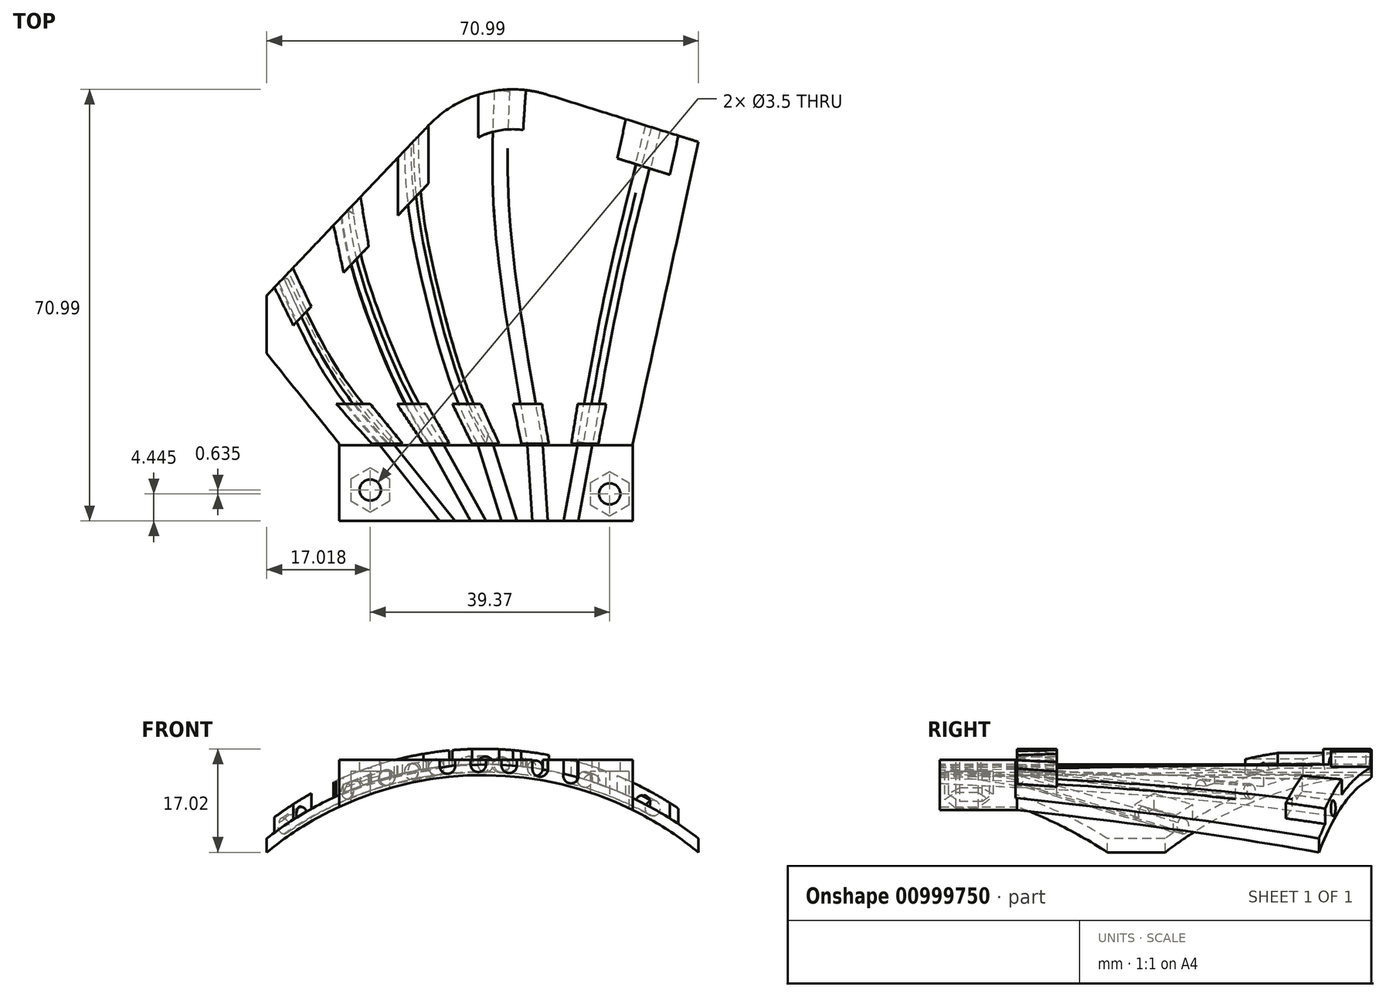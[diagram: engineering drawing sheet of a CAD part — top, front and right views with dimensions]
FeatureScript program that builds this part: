
annotation { "Feature Type Name" : "Feature", "Feature Type Description" : "" }
export const myFeature = defineFeature(function(context is Context, id is Id, definition is map)
    precondition{}
    {
        {
            var Q0;
            Q0=qCreatedBy(makeId("Front.planeOp"),FACE);
            var sketch = newSketch(context, id + "F0", { "sketchPlane" : qUnion([Q0])});
            skLineSegment(sketch, "E0", {"start": v(0, 0) * mm, "end": v(71, 0) * mm});
            skLineSegment(sketch, "E1", {"start": v(35.5, 0) * mm, "end": v(35.5, 12.7) * mm});
            skArc(sketch, "E2", {"start": v(71, 0) * mm, "mid": v(35.5, 12.7) * mm, "end": v(0, 0) * mm});
            skArc(sketch, "E3.0", {"start": v(71, 2.28) * mm, "mid": v(35.5, 14.48) * mm, "end": v(0, 2.28) * mm});
            skLineSegment(sketch, "E4", {"start": v(0, 0) * mm, "end": v(0, 2.28) * mm});
            skLineSegment(sketch, "E5", {"start": v(71, 0) * mm, "end": v(71, 2.28) * mm});
            skSolve(sketch);
        }
        {
            var Q0;
            Q0=makeQuery(id+"F0.imprint","IMPRINT",FACE,{"disambiguationData":[TD([[makeQuery(id+"F0.imprint","IMPRINT",EDGE,{"derivedFrom":sQuery(id+"F0.wireOp",EDGE,"E3.0")}),1.0]])]});
            extrude(context, id + "F1", {"entities" : qUnion([Q0]), "oppositeDirection" : true, "depth" : 63.5 * mm, "offsetDistance" : 25.4 * mm});
        }
        {
            var Q0;
            Q0=qCreatedBy(makeId("Top.planeOp"),FACE);
            cPlane(context, id + "F2", {"entities" : qUnion([Q0]), "cplaneType" : CPlaneType.OFFSET, "offset" : 25.4 * mm, "width" : 152.4 * mm, "height" : 152.4 * mm});
        }
        {
            var Q0;
            Q0=qCreatedBy(id+"F2.planeOp",FACE);
            var sketch = newSketch(context, id + "F3", { "sketchPlane" : qUnion([Q0])});
            skLineSegment(sketch, "E6", {"start": v(11.94, 0) * mm, "end": v(60.2, 0) * mm});
            skLineSegment(sketch, "E7", {"start": v(60.2, 0) * mm, "end": v(71, 49.64) * mm});
            skLineSegment(sketch, "E8", {"start": v(11.94, 0) * mm, "end": v(0, 14.85) * mm});
            skLineSegment(sketch, "E9", {"start": v(0, 14.85) * mm, "end": v(0, 24.37) * mm});
            skLineSegment(sketch, "E10", {"start": v(0, 24.37) * mm, "end": v(26.63, 52.37) * mm});
            skLineSegment(sketch, "E11", {"start": v(46.12, 57.42) * mm, "end": v(71, 49.64) * mm});
            skPoint(sketch, "E12.visualSharp", {"position": v(34.8, 60.96) * mm});
            skArc(sketch, "E12.filletArc", {"start": v(46.12, 57.42) * mm, "mid": v(35.65, 57.68) * mm, "end": v(26.63, 52.37) * mm});
            skLineSegment(sketch, "E13.0", {"start": v(71, 63.5) * mm, "end": v(0, 63.5) * mm});
            skLineSegment(sketch, "E14.bottom", {"start": v(0, 0) * mm, "end": v(71, 0) * mm});
            skLineSegment(sketch, "E14.top", {"start": v(0, 63.5) * mm, "end": v(71, 63.5) * mm});
            skLineSegment(sketch, "E14.left", {"start": v(0, 0) * mm, "end": v(0, 63.5) * mm});
            skLineSegment(sketch, "E14.right", {"start": v(71, 0) * mm, "end": v(71, 63.5) * mm});
            skSolve(sketch);
        }
        {
            var Q0;
            {var subQ2=sQuery(id+"F3.wireOp",EDGE,"E10");Q0=makeQuery(id+"F3.imprint","IMPRINT",FACE,{"disambiguationData":[TD([[makeQuery(id+"F3.imprint","IMPRINT",EDGE,{"derivedFrom":subQ2}),1.0]])]});}
            var Q1;
            {var subQ0=sQuery(id+"F3.wireOp",EDGE,"E7");Q1=makeQuery(id+"F3.imprint","IMPRINT",FACE,{"disambiguationData":[TD([[makeQuery(id+"F3.imprint","IMPRINT",EDGE,{"derivedFrom":subQ0}),-1.0]])]});}
            var Q2;
            {var subQ0=sQuery(id+"F3.wireOp",EDGE,"E8");Q2=makeQuery(id+"F3.imprint","IMPRINT",FACE,{"disambiguationData":[TD([[makeQuery(id+"F3.imprint","IMPRINT",EDGE,{"derivedFrom":subQ0}),1.0]])]});}
            extrude(context, id + "F4", {"entities" : qUnion([Q0, Q1, Q2]), "operationType" : NewBodyOperationType.REMOVE, "oppositeDirection" : true, "depth" : 25.4 * mm, "offsetDistance" : 25.4 * mm});
        }
        {
            var Q0;
            Q0=qCreatedBy(id+"F2.planeOp",FACE);
            var sketch = newSketch(context, id + "F5", { "sketchPlane" : qUnion([Q0])});
            skPoint(sketch, "E15.0", {"position": v(0, 14.85) * mm});
            skLineSegment(sketch, "E16", {"start": v(0, 14.85) * mm, "end": v(26.63, 42.84) * mm});
            skLineSegment(sketch, "E17", {"start": v(26.63, 52.37) * mm, "end": v(26.63, 42.84) * mm});
            skLineSegment(sketch, "E18", {"start": v(61.63, 6.56) * mm, "end": v(6.66, 6.56) * mm});
            skLineSegment(sketch, "E19.0", {"start": v(57.66, 46.93) * mm, "end": v(66.3, 44.23) * mm});
            skArc(sketch, "E19.1", {"start": v(42.17, 51.6) * mm, "mid": v(38.39, 51.56) * mm, "end": v(34.8, 50.38) * mm});
            skLineSegment(sketch, "E20", {"start": v(42.17, 51.6) * mm, "end": v(42.6, 58.16) * mm});
            skLineSegment(sketch, "E21", {"start": v(34.8, 50.38) * mm, "end": v(34.8, 57.44) * mm});
            skLineSegment(sketch, "E22", {"start": v(67.7, 50.67) * mm, "end": v(66.3, 44.23) * mm});
            skLineSegment(sketch, "E23", {"start": v(59.06, 53.37) * mm, "end": v(57.66, 46.93) * mm});
            skLineSegment(sketch, "E24.0", {"start": v(0, 24.37) * mm, "end": v(26.63, 52.37) * mm});
            skLineSegment(sketch, "E25.0", {"start": v(60.2, 0) * mm, "end": v(11.94, 0) * mm});
            skLineSegment(sketch, "E26.0.1", {"start": v(0, 24.37) * mm, "end": v(0, 14.85) * mm});
            skLineSegment(sketch, "E26.0.2", {"start": v(11.94, 0) * mm, "end": v(0, 14.85) * mm});
            skLineSegment(sketch, "E26.0.3", {"start": v(11.94, 0) * mm, "end": v(60.2, 0) * mm});
            skLineSegment(sketch, "E26.0.4", {"start": v(60.2, 0) * mm, "end": v(71, 49.64) * mm});
            skLineSegment(sketch, "E26.0.5", {"start": v(46.12, 57.42) * mm, "end": v(71, 49.64) * mm});
            skArc(sketch, "E26.0.6", {"start": v(46.12, 57.42) * mm, "mid": v(35.65, 57.68) * mm, "end": v(26.63, 52.37) * mm});
            skPoint(sketch, "E27", {"position": v(19.98, 0) * mm});
            skPoint(sketch, "E28.1.0.0", {"position": v(28.02, 0) * mm});
            skPoint(sketch, "E28.2.0.0", {"position": v(36.07, 0) * mm});
            skPoint(sketch, "E28.3.0.0", {"position": v(44.11, 0) * mm});
            skPoint(sketch, "E28.4.0.0", {"position": v(52.15, 0) * mm});
            skLineSegment(sketch, "E28.direction1", {"start": v(19.98, 0) * mm, "end": v(28.02, 0) * mm, "construction": true});
            skPoint(sketch, "E29", {"position": v(63.38, 52.02) * mm});
            skPoint(sketch, "E30.visualSharp", {"position": v(34.8, 60.96) * mm});
            skPoint(sketch, "E31", {"position": v(38.66, 58.2) * mm});
            skLineSegment(sketch, "E32", {"start": v(26.63, 52.37) * mm, "end": v(0, 24.37) * mm});
            skPoint(sketch, "E33", {"position": v(13.31, 38.37) * mm});
            skPoint(sketch, "E34", {"position": v(23.82, 49.41) * mm});
            skPoint(sketch, "E35", {"position": v(2.81, 27.33) * mm});
            skFitSpline(sketch, "E36", {"points": [v(63.38, 52.02) * mm, v(57.3, 27.29) * mm, v(52.15, 0) * mm], "startDerivative": vector(-13.01, -49.86) * mm, "endDerivative": vector(-9.46, -54.16) * mm});
            skFitSpline(sketch, "E37", {"points": [v(38.66, 58.2) * mm, v(38.66, 37.31) * mm, v(44.11, 0) * mm], "startDerivative": vector(-2.03, -45.53) * mm, "endDerivative": vector(12.23, -69.7) * mm});
            skFitSpline(sketch, "E38", {"points": [v(23.82, 49.41) * mm, v(27.68, 22.82) * mm, v(36.07, 0) * mm], "startDerivative": vector(-0.7, -55.32) * mm, "endDerivative": vector(25.48, -43.38) * mm});
            skFitSpline(sketch, "E39", {"points": [v(13.31, 38.37) * mm, v(18.34, 19.33) * mm, v(28.02, 0) * mm], "startDerivative": vector(3.78, -39.84) * mm, "endDerivative": vector(25.36, -36.93) * mm});
            skFitSpline(sketch, "E40", {"points": [v(2.81, 27.33) * mm, v(10.9, 11.48) * mm, v(19.98, 0) * mm], "startDerivative": vector(14.48, -31.8) * mm, "endDerivative": vector(19.95, -22.7) * mm});
            skLineSegment(sketch, "E41", {"start": v(21.6, 47.07) * mm, "end": v(21.6, 37.55) * mm});
            skLineSegment(sketch, "E42", {"start": v(15.42, 40.58) * mm, "end": v(16.78, 32.5) * mm});
            skLineSegment(sketch, "E43", {"start": v(10.99, 35.92) * mm, "end": v(12.65, 28.15) * mm});
            skLineSegment(sketch, "E44", {"start": v(4.3, 28.9) * mm, "end": v(7.33, 22.55) * mm});
            skLineSegment(sketch, "E45", {"start": v(4.39, 19.46) * mm, "end": v(1.27, 25.7) * mm});
            skLineSegment(sketch, "E46", {"start": v(45.25, 6.56) * mm, "end": v(46.39, 0) * mm});
            skLineSegment(sketch, "E47", {"start": v(40.53, 6.56) * mm, "end": v(41.87, 0) * mm});
            skLineSegment(sketch, "E48", {"start": v(35.2, 6.56) * mm, "end": v(38.22, 0) * mm});
            skLineSegment(sketch, "E49", {"start": v(30.5, 6.56) * mm, "end": v(33.76, 0) * mm});
            skLineSegment(sketch, "E50", {"start": v(26.28, 6.56) * mm, "end": v(30.05, 0) * mm});
            skLineSegment(sketch, "E51", {"start": v(21.43, 6.56) * mm, "end": v(25.76, 0) * mm});
            skLineSegment(sketch, "E52", {"start": v(17, 6.56) * mm, "end": v(22.34, 0) * mm});
            skLineSegment(sketch, "E53", {"start": v(11.4, 6.56) * mm, "end": v(17.27, 0) * mm});
            skLineSegment(sketch, "E54", {"start": v(55.82, 6.56) * mm, "end": v(54.53, 0) * mm});
            skLineSegment(sketch, "E55", {"start": v(51.14, 6.56) * mm, "end": v(50.09, 0) * mm});
            skSolve(sketch);
        }
        {
            var Q0;
            {var subQ2=sQuery(id+"F5.wireOp",EDGE,"83fa2006-919e-4d0e-9ed9-299d969f0d94.0");Q0=makeQuery(id+"F5.imprint","IMPRINT",FACE,{"disambiguationData":[TD([[makeQuery(id+"F5.imprint","IMPRINT",EDGE,{"derivedFrom":subQ2}),1.0]])]});}
            var Q1;
            {var subQ0=sQuery(id+"F5.wireOp",EDGE,"3e86846c-4f64-452c-aa2e-ba2f01902673.0");Q1=makeQuery(id+"F5.imprint","IMPRINT",FACE,{"disambiguationData":[TD([[makeQuery(id+"F5.imprint","IMPRINT",EDGE,{"derivedFrom":subQ0}),-1.0]])]});}
            var Q2;
            {var subQ0=sQuery(id+"F5.wireOp",EDGE,"E17");Q2=makeQuery(id+"F5.imprint","IMPRINT",FACE,{"disambiguationData":[TD([[makeQuery(id+"F5.imprint","IMPRINT",EDGE,{"derivedFrom":subQ0}),-1.0]])]});}
            var Q3;
            Q3=makeQuery(id+"F5.imprint","IMPRINT",FACE,{"disambiguationData":[TD([[makeQuery(id+"F5.imprint","IMPRINT",EDGE,{"derivedFrom":sQuery(id+"F5.wireOp",EDGE,"E19.1")}),-1.0]])]});
            var Q4;
            Q4=makeQuery(id+"F5.imprint","IMPRINT",FACE,{"disambiguationData":[TD([[makeQuery(id+"F5.imprint","IMPRINT",EDGE,{"derivedFrom":sQuery(id+"F5.wireOp",EDGE,"E19.0")}),1.0]])]});
            var Q5;
            {var subQ0=sQuery(id+"F5.wireOp",EDGE,"b734ba61-1a13-4ae3-a532-8137c9726fd6.0");Q5=makeQuery(id+"F5.imprint","IMPRINT",FACE,{"disambiguationData":[TD([[makeQuery(id+"F5.imprint","IMPRINT",EDGE,{"derivedFrom":subQ0}),-1.0]])]});}
            var Q6;
            {var subQ0=sQuery(id+"F5.wireOp",EDGE,"2f5c6003-4ff3-49cd-9c1d-814e9e2b850a.0");Q6=makeQuery(id+"F5.imprint","IMPRINT",FACE,{"disambiguationData":[TD([[makeQuery(id+"F5.imprint","IMPRINT",EDGE,{"derivedFrom":subQ0}),-1.0]])]});}
            var Q7;
            {var subQ0=sQuery(id+"F5.wireOp",EDGE,"77d394c1-dc6a-4f35-b963-1066929f6d7f.0");Q7=makeQuery(id+"F5.imprint","IMPRINT",FACE,{"disambiguationData":[TD([[makeQuery(id+"F5.imprint","IMPRINT",EDGE,{"derivedFrom":subQ0}),-1.0]])]});}
            var Q8;
            {var subQ0=sQuery(id+"F5.wireOp",EDGE,"7f80335d-9f36-4739-b935-51cdfa12f308.0");Q8=makeQuery(id+"F5.imprint","IMPRINT",FACE,{"disambiguationData":[TD([[makeQuery(id+"F5.imprint","IMPRINT",EDGE,{"derivedFrom":subQ0}),-1.0]])]});}
            var Q9;
            {var subQ0=sQuery(id+"F5.wireOp",EDGE,"81e54f59-7b8b-4100-84fe-d6a8937c8e77.0");Q9=makeQuery(id+"F5.imprint","IMPRINT",FACE,{"disambiguationData":[TD([[makeQuery(id+"F5.imprint","IMPRINT",EDGE,{"derivedFrom":subQ0}),-1.0]])]});}
            var Q10;
            {var subQ0=sQuery(id+"F5.wireOp",EDGE,"E41");Q10=makeQuery(id+"F5.imprint","IMPRINT",FACE,{"disambiguationData":[TD([[makeQuery(id+"F5.imprint","IMPRINT",EDGE,{"derivedFrom":subQ0}),1.0]])]});}
            var Q11;
            {var subQ0=sQuery(id+"F5.wireOp",EDGE,"E42");Q11=makeQuery(id+"F5.imprint","IMPRINT",FACE,{"disambiguationData":[TD([[makeQuery(id+"F5.imprint","IMPRINT",EDGE,{"derivedFrom":subQ0}),-1.0]])]});}
            var Q12;
            {var subQ0=sQuery(id+"F5.wireOp",EDGE,"E43");Q12=makeQuery(id+"F5.imprint","IMPRINT",FACE,{"disambiguationData":[TD([[makeQuery(id+"F5.imprint","IMPRINT",EDGE,{"derivedFrom":subQ0}),1.0]])]});}
            var Q13;
            {var subQ0=sQuery(id+"F5.wireOp",EDGE,"E44");Q13=makeQuery(id+"F5.imprint","IMPRINT",FACE,{"disambiguationData":[TD([[makeQuery(id+"F5.imprint","IMPRINT",EDGE,{"derivedFrom":subQ0}),-1.0]])]});}
            var Q14;
            {var subQ0=sQuery(id+"F5.wireOp",EDGE,"E45");Q14=makeQuery(id+"F5.imprint","IMPRINT",FACE,{"disambiguationData":[TD([[makeQuery(id+"F5.imprint","IMPRINT",EDGE,{"derivedFrom":subQ0}),-1.0]])]});}
            var Q15;
            {var subQ0=sQuery(id+"F5.wireOp",EDGE,"E53");Q15=makeQuery(id+"F5.imprint","IMPRINT",FACE,{"disambiguationData":[TD([[makeQuery(id+"F5.imprint","IMPRINT",EDGE,{"derivedFrom":subQ0}),1.0]])]});}
            var Q16;
            {var subQ0=sQuery(id+"F5.wireOp",EDGE,"E52");Q16=makeQuery(id+"F5.imprint","IMPRINT",FACE,{"disambiguationData":[TD([[makeQuery(id+"F5.imprint","IMPRINT",EDGE,{"derivedFrom":subQ0}),-1.0]])]});}
            var Q17;
            {var subQ0=sQuery(id+"F5.wireOp",EDGE,"E51");Q17=makeQuery(id+"F5.imprint","IMPRINT",FACE,{"disambiguationData":[TD([[makeQuery(id+"F5.imprint","IMPRINT",EDGE,{"derivedFrom":subQ0}),1.0]])]});}
            var Q18;
            {var subQ0=sQuery(id+"F5.wireOp",EDGE,"E50");Q18=makeQuery(id+"F5.imprint","IMPRINT",FACE,{"disambiguationData":[TD([[makeQuery(id+"F5.imprint","IMPRINT",EDGE,{"derivedFrom":subQ0}),-1.0]])]});}
            var Q19;
            {var subQ0=sQuery(id+"F5.wireOp",EDGE,"E48");Q19=makeQuery(id+"F5.imprint","IMPRINT",FACE,{"disambiguationData":[TD([[makeQuery(id+"F5.imprint","IMPRINT",EDGE,{"derivedFrom":subQ0}),-1.0]])]});}
            var Q20;
            {var subQ0=sQuery(id+"F5.wireOp",EDGE,"E49");Q20=makeQuery(id+"F5.imprint","IMPRINT",FACE,{"disambiguationData":[TD([[makeQuery(id+"F5.imprint","IMPRINT",EDGE,{"derivedFrom":subQ0}),1.0]])]});}
            var Q21;
            {var subQ0=sQuery(id+"F5.wireOp",EDGE,"E47");Q21=makeQuery(id+"F5.imprint","IMPRINT",FACE,{"disambiguationData":[TD([[makeQuery(id+"F5.imprint","IMPRINT",EDGE,{"derivedFrom":subQ0}),1.0]])]});}
            var Q22;
            {var subQ0=sQuery(id+"F5.wireOp",EDGE,"E46");Q22=makeQuery(id+"F5.imprint","IMPRINT",FACE,{"disambiguationData":[TD([[makeQuery(id+"F5.imprint","IMPRINT",EDGE,{"derivedFrom":subQ0}),-1.0]])]});}
            var Q23;
            {var subQ0=sQuery(id+"F5.wireOp",EDGE,"E55");Q23=makeQuery(id+"F5.imprint","IMPRINT",FACE,{"disambiguationData":[TD([[makeQuery(id+"F5.imprint","IMPRINT",EDGE,{"derivedFrom":subQ0}),1.0]])]});}
            var Q24;
            {var subQ0=sQuery(id+"F5.wireOp",EDGE,"E54");Q24=makeQuery(id+"F5.imprint","IMPRINT",FACE,{"disambiguationData":[TD([[makeQuery(id+"F5.imprint","IMPRINT",EDGE,{"derivedFrom":subQ0}),-1.0]])]});}
            var Q25;
            Q25=makeQuery(id+"F1.opExtrude","SWEPT_FACE",FACE,{"disambiguationData":[OSD([sQuery(id+"F0.wireOp",EDGE,"E3.0")])]});
            extrude(context, id + "F6", {"entities" : qUnion([Q0, Q1, Q2, Q3, Q4, Q5, Q6, Q7, Q8, Q9, Q10, Q11, Q12, Q13, Q14, Q15, Q16, Q17, Q18, Q19, Q20, Q21, Q22, Q23, Q24]), "operationType" : NewBodyOperationType.ADD, "endBound" : BoundingType.UP_TO_SURFACE, "oppositeDirection" : true, "depth" : 25.4 * mm, "endBoundEntityFace" : qUnion([Q25]), "offsetDistance" : 25.4 * mm});
        }
        {
            var Q0;
            Q0=qCreatedBy(makeId("Front.planeOp"),FACE);
            var sketch = newSketch(context, id + "F7", { "sketchPlane" : qUnion([Q0])});
            skArc(sketch, "E56.0", {"start": v(11.94, 9.45) * mm, "mid": v(5.75, 6.23) * mm, "end": v(0, 2.28) * mm});
            skArc(sketch, "E57.0", {"start": v(17.27, 11.52) * mm, "mid": v(14.58, 10.55) * mm, "end": v(11.94, 9.45) * mm});
            skArc(sketch, "E58.0", {"start": v(60.2, 8.93) * mm, "mid": v(65.78, 5.9) * mm, "end": v(71, 2.28) * mm});
            skArc(sketch, "E59", {"start": v(71, 2.28) * mm, "mid": v(35.5, 14.48) * mm, "end": v(0, 2.28) * mm});
            skArc(sketch, "E60", {"start": v(71, 4.82) * mm, "mid": v(35.5, 17.02) * mm, "end": v(0, 4.82) * mm});
            skLineSegment(sketch, "E61", {"start": v(71, 2.28) * mm, "end": v(71, 4.05) * mm});
            skLineSegment(sketch, "E62", {"start": v(0, 2.28) * mm, "end": v(0, 4.05) * mm});
            skPoint(sketch, "E63.0", {"position": v(26.63, 25.4) * mm});
            skLineSegment(sketch, "E64", {"start": v(71, 25.4) * mm, "end": v(71, 4.05) * mm});
            skLineSegment(sketch, "E65", {"start": v(71, 25.4) * mm, "end": v(0, 25.4) * mm});
            skLineSegment(sketch, "E66", {"start": v(0, 25.4) * mm, "end": v(0, 4.05) * mm});
            skSolve(sketch);
        }
        {
            var Q0;
            Q0=makeQuery(id+"F7.imprint","IMPRINT",FACE,{"disambiguationData":[TD([[makeQuery(id+"F7.imprint","IMPRINT",EDGE,{"derivedFrom":sQuery(id+"F7.wireOp",EDGE,"E60")}),-1.0]])]});
            extrude(context, id + "F8", {"entities" : qUnion([Q0]), "operationType" : NewBodyOperationType.REMOVE, "endBound" : BoundingType.THROUGH_ALL, "oppositeDirection" : true, "depth" : 25.4 * mm, "offsetDistance" : 25.4 * mm});
        }
        {
            var Q0;
            Q0=qCreatedBy(id+"F2.planeOp",FACE);
            var sketch = newSketch(context, id + "F9", { "sketchPlane" : qUnion([Q0])});
            skPoint(sketch, "E67.0", {"position": v(0, 24.37) * mm});
            skPoint(sketch, "E68", {"position": v(19.98, 0) * mm});
            skPoint(sketch, "E69.1.0.0", {"position": v(28.02, 0) * mm});
            skPoint(sketch, "E69.2.0.0", {"position": v(36.07, 0) * mm});
            skPoint(sketch, "E69.3.0.0", {"position": v(44.11, 0) * mm});
            skPoint(sketch, "E69.4.0.0", {"position": v(52.15, 0) * mm});
            skPoint(sketch, "E70", {"position": v(63.38, 52.02) * mm});
            skPoint(sketch, "E71.visualSharp", {"position": v(34.8, 60.96) * mm});
            skPoint(sketch, "E72", {"position": v(38.66, 58.2) * mm});
            skPoint(sketch, "E73", {"position": v(13.31, 38.37) * mm});
            skPoint(sketch, "E74", {"position": v(23.82, 49.41) * mm});
            skPoint(sketch, "E75", {"position": v(2.81, 27.33) * mm});
            skFitSpline(sketch, "E76", {"points": [v(63.38, 52.02) * mm, v(57.3, 27.29) * mm, v(52.15, 0) * mm], "startDerivative": vector(-13.01, -49.86) * mm, "endDerivative": vector(-9.46, -54.16) * mm});
            skFitSpline(sketch, "E77", {"points": [v(38.66, 58.2) * mm, v(38.66, 37.31) * mm, v(44.11, 0) * mm], "startDerivative": vector(-2.03, -45.53) * mm, "endDerivative": vector(12.23, -69.7) * mm});
            skFitSpline(sketch, "E78", {"points": [v(23.82, 49.41) * mm, v(27.68, 22.82) * mm, v(36.07, 0) * mm], "startDerivative": vector(-0.7, -55.32) * mm, "endDerivative": vector(25.48, -43.38) * mm});
            skFitSpline(sketch, "E79", {"points": [v(13.31, 38.37) * mm, v(18.34, 19.33) * mm, v(28.02, 0) * mm], "startDerivative": vector(3.78, -39.84) * mm, "endDerivative": vector(25.36, -36.93) * mm});
            skFitSpline(sketch, "E80", {"points": [v(2.81, 27.33) * mm, v(10.9, 11.48) * mm, v(19.98, 0) * mm], "startDerivative": vector(14.48, -31.8) * mm, "endDerivative": vector(19.95, -22.7) * mm});
            skSolve(sketch);
        }
        {
            var Q0;
            {var subQ0=sQuery(id+"F5.wireOp",EDGE,"E26.0.3");var subQ1=makeQuery(id+"F5.imprint","INTERSECT",VERTEX,{"derivedFrom":[subQ0,sQuery(id+"F5.wireOp",EDGE,"E36")]});var subQ2=makeQuery(id+"F5.imprint","INTERSECT",VERTEX,{"derivedFrom":[subQ0,sQuery(id+"F5.wireOp",EDGE,"E37")]});var subQ3=makeQuery(id+"F5.imprint","INTERSECT",VERTEX,{"derivedFrom":[subQ0,sQuery(id+"F5.wireOp",EDGE,"E38")]});var subQ4=makeQuery(id+"F5.imprint","INTERSECT",VERTEX,{"derivedFrom":[subQ0,sQuery(id+"F5.wireOp",EDGE,"E39")]});var subQ5=makeQuery(id+"F5.imprint","INTERSECT",VERTEX,{"derivedFrom":[subQ0,sQuery(id+"F5.wireOp",EDGE,"E40")]});Q0=makeQuery(id+"F6.boolean.opBoolean","MERGE",FACE,{"derivedFrom":[makeQuery(id+"F1.opExtrude","CAP_FACE",FACE,{"disambiguationData":[OSD([sQuery(id+"F0.wireOp",EDGE,"E2"),sQuery(id+"F0.wireOp",EDGE,"E3.0"),sQuery(id+"F0.wireOp",EDGE,"E4"),sQuery(id+"F0.wireOp",EDGE,"E5")])],"isStart":true}),makeQuery(id+"F6.opExtrude","SWEPT_FACE",FACE,{"disambiguationData":[OSD([subQ0]),TDD([makeQuery(id+"F5.imprint","IMPRINT",EDGE,{"disambiguationData":[TD([[subQ5,1.0]])],"derivedFrom":subQ0}),makeQuery(id+"F5.imprint","IMPRINT",EDGE,{"disambiguationData":[TD([[subQ5,-1.0]])],"derivedFrom":subQ0})])]}),makeQuery(id+"F6.opExtrude","SWEPT_FACE",FACE,{"disambiguationData":[OSD([subQ0]),TDD([makeQuery(id+"F5.imprint","IMPRINT",EDGE,{"disambiguationData":[TD([[subQ4,1.0]])],"derivedFrom":subQ0}),makeQuery(id+"F5.imprint","IMPRINT",EDGE,{"disambiguationData":[TD([[subQ4,-1.0]])],"derivedFrom":subQ0})])]}),makeQuery(id+"F6.opExtrude","SWEPT_FACE",FACE,{"disambiguationData":[OSD([subQ0]),TDD([makeQuery(id+"F5.imprint","IMPRINT",EDGE,{"disambiguationData":[TD([[subQ3,1.0]])],"derivedFrom":subQ0}),makeQuery(id+"F5.imprint","IMPRINT",EDGE,{"disambiguationData":[TD([[subQ3,-1.0]])],"derivedFrom":subQ0})])]}),makeQuery(id+"F6.opExtrude","SWEPT_FACE",FACE,{"disambiguationData":[OSD([subQ0]),TDD([makeQuery(id+"F5.imprint","IMPRINT",EDGE,{"disambiguationData":[TD([[subQ2,1.0]])],"derivedFrom":subQ0}),makeQuery(id+"F5.imprint","IMPRINT",EDGE,{"disambiguationData":[TD([[subQ2,-1.0]])],"derivedFrom":subQ0})])]}),makeQuery(id+"F6.opExtrude","SWEPT_FACE",FACE,{"disambiguationData":[OSD([subQ0]),TDD([makeQuery(id+"F5.imprint","IMPRINT",EDGE,{"disambiguationData":[TD([[subQ1,1.0]])],"derivedFrom":subQ0}),makeQuery(id+"F5.imprint","IMPRINT",EDGE,{"disambiguationData":[TD([[subQ1,-1.0]])],"derivedFrom":subQ0})])]})]});}
            var sketch = newSketch(context, id + "F10", { "sketchPlane" : qUnion([Q0])});
            skPoint(sketch, "E81.centerSnap0", {"position": v(19.79, 14.84) * mm});
            skLineSegment(sketch, "E82", {"start": v(17.27, 14.06) * mm, "end": v(17.27, 12.29) * mm});
            skLineSegment(sketch, "E83", {"start": v(22.34, 15.5) * mm, "end": v(22.34, 13.72) * mm});
            skLineSegment(sketch, "E84", {"start": v(25.76, 16.2) * mm, "end": v(25.76, 14.41) * mm});
            skLineSegment(sketch, "E85", {"start": v(30.05, 16.76) * mm, "end": v(30.05, 14.98) * mm});
            skLineSegment(sketch, "E86", {"start": v(33.76, 17) * mm, "end": v(33.76, 15.21) * mm});
            skLineSegment(sketch, "E87", {"start": v(38.22, 16.95) * mm, "end": v(38.22, 15.18) * mm});
            skLineSegment(sketch, "E88", {"start": v(41.87, 16.67) * mm, "end": v(41.87, 14.13) * mm});
            skLineSegment(sketch, "E89", {"start": v(46.39, 15.98) * mm, "end": v(46.39, 14.2) * mm});
            skLineSegment(sketch, "E90", {"start": v(50.09, 15.14) * mm, "end": v(50.09, 13.37) * mm});
            skLineSegment(sketch, "E91", {"start": v(54.53, 13.8) * mm, "end": v(54.53, 11.25) * mm});
            skCircle(sketch, "E92", {"center": v(19.79, 12.3) * mm, "radius": 1.27 * mm});
            skCircle(sketch, "E93", {"center": v(27.9, 13.98) * mm, "radius": 1.27 * mm});
            skCircle(sketch, "E94", {"center": v(36, 14.48) * mm, "radius": 1.27 * mm});
            skCircle(sketch, "E95", {"center": v(44.13, 13.83) * mm, "radius": 1.27 * mm});
            skCircle(sketch, "E96", {"center": v(52.32, 11.97) * mm, "radius": 1.27 * mm});
            skSolve(sketch);
        }
        {
            var Q0;
            Q0=makeQuery(id+"F6.boolean.opBoolean","MERGE",FACE,{"derivedFrom":[makeQuery(id+"F4.boolean.opBoolean","COPY",FACE,{"derivedFrom":makeQuery(id+"F4.opExtrude","SWEPT_FACE",FACE,{"disambiguationData":[OSD([sQuery(id+"F3.wireOp",EDGE,"E11")])]})}),makeQuery(id+"F6.opExtrude","SWEPT_FACE",FACE,{"disambiguationData":[OSD([sQuery(id+"F5.wireOp",EDGE,"E26.0.5")])]})]});
            var sketch = newSketch(context, id + "F11", { "sketchPlane" : qUnion([Q0])});
            skLineSegment(sketch, "E97", {"start": v(-49.49, 7.2) * mm, "end": v(-49.49, 5.42) * mm});
            skLineSegment(sketch, "E98", {"start": v(-40.43, 12) * mm, "end": v(-40.43, 10.21) * mm});
            skCircle(sketch, "E99", {"center": v(-45.06, 7.24) * mm, "radius": 1.27 * mm});
            skSolve(sketch);
        }
        {
            var Q0;
            {var subQ0=sQuery(id+"F5.wireOp",EDGE,"E32");var subQ1=makeQuery(id+"F5.imprint","INTERSECT",VERTEX,{"derivedFrom":[subQ0,sQuery(id+"F5.wireOp",EDGE,"E40")]});var subQ2=makeQuery(id+"F5.imprint","INTERSECT",VERTEX,{"derivedFrom":[subQ0,sQuery(id+"F5.wireOp",EDGE,"E39")]});var subQ3=makeQuery(id+"F5.imprint","INTERSECT",VERTEX,{"derivedFrom":[subQ0,sQuery(id+"F5.wireOp",EDGE,"E38")]});Q0=makeQuery(id+"F6.boolean.opBoolean","MERGE",FACE,{"derivedFrom":[makeQuery(id+"F4.boolean.opBoolean","COPY",FACE,{"derivedFrom":makeQuery(id+"F4.opExtrude","SWEPT_FACE",FACE,{"disambiguationData":[OSD([sQuery(id+"F3.wireOp",EDGE,"E10")])]})}),makeQuery(id+"F6.opExtrude","SWEPT_FACE",FACE,{"disambiguationData":[OSD([subQ0]),TDD([makeQuery(id+"F5.imprint","IMPRINT",EDGE,{"disambiguationData":[TD([[subQ3,1.0]])],"derivedFrom":subQ0}),makeQuery(id+"F5.imprint","IMPRINT",EDGE,{"disambiguationData":[TD([[subQ3,-1.0]])],"derivedFrom":subQ0})])]}),makeQuery(id+"F6.opExtrude","SWEPT_FACE",FACE,{"disambiguationData":[OSD([subQ0]),TDD([makeQuery(id+"F5.imprint","IMPRINT",EDGE,{"disambiguationData":[TD([[subQ2,1.0]])],"derivedFrom":subQ0}),makeQuery(id+"F5.imprint","IMPRINT",EDGE,{"disambiguationData":[TD([[subQ2,-1.0]])],"derivedFrom":subQ0})])]}),makeQuery(id+"F6.opExtrude","SWEPT_FACE",FACE,{"disambiguationData":[OSD([subQ0]),TDD([makeQuery(id+"F5.imprint","IMPRINT",EDGE,{"disambiguationData":[TD([[subQ1,1.0]])],"derivedFrom":subQ0}),makeQuery(id+"F5.imprint","IMPRINT",EDGE,{"disambiguationData":[TD([[subQ1,-1.0]])],"derivedFrom":subQ0})])]})]});}
            var sketch = newSketch(context, id + "F12", { "sketchPlane" : qUnion([Q0])});
            skLineSegment(sketch, "E100", {"start": v(-48.99, 15.32) * mm, "end": v(-48.99, 13.58) * mm});
            skLineSegment(sketch, "E101", {"start": v(-40.03, 13.41) * mm, "end": v(-40.03, 11.67) * mm});
            skLineSegment(sketch, "E102", {"start": v(-33.6, 11.56) * mm, "end": v(-33.6, 9.78) * mm});
            skLineSegment(sketch, "E103", {"start": v(-23.9, 7.86) * mm, "end": v(-23.9, 6.05) * mm});
            skLineSegment(sketch, "E104", {"start": v(-19.5, 5.78) * mm, "end": v(-19.5, 3.98) * mm});
            skCircle(sketch, "E105", {"center": v(-52.63, 13.37) * mm, "radius": 1.27 * mm});
            skCircle(sketch, "E106", {"center": v(-36.8, 10.01) * mm, "radius": 1.27 * mm});
            skCircle(sketch, "E107", {"center": v(-21.69, 4.28) * mm, "radius": 1.27 * mm});
            skSolve(sketch);
        }
        {
            var Q0;
            Q0=qSketchRegion(id+"F9",true);
            var Q1;
            Q1=sQuery(id+"F9.wireOp",EDGE,"E76");
            var Q2;
            Q2=sQuery(id+"F9.wireOp",EDGE,"E77");
            var Q3;
            Q3=sQuery(id+"F9.wireOp",EDGE,"E78");
            var Q4;
            Q4=sQuery(id+"F9.wireOp",EDGE,"E79");
            var Q5;
            Q5=sQuery(id+"F9.wireOp",EDGE,"E80");
            var Q6;
            Q6=makeQuery(id+"F1.opExtrude","SWEPT_FACE",FACE,{"disambiguationData":[OSD([sQuery(id+"F0.wireOp",EDGE,"E3.0")])]});
            extrude(context, id + "F13", {"entities" : qUnion([Q0]), "bodyType" : ToolBodyType.SURFACE, "surfaceEntities" : qUnion([Q1, Q2, Q3, Q4, Q5]), "endBound" : BoundingType.UP_TO_SURFACE, "oppositeDirection" : true, "depth" : 25.4 * mm, "endBoundEntityFace" : qUnion([Q6]), "offsetDistance" : 25.4 * mm});
        }
        {
            var Q0;
            Q0=makeQuery(id+"F11.imprint","IMPRINT",FACE,{"disambiguationData":[TD([[makeQuery(id+"F11.imprint","IMPRINT",EDGE,{"derivedFrom":sQuery(id+"F11.wireOp",EDGE,"E99")}),1.0]])]});
            var Q1;
            Q1=makeQuery(id+"F10.imprint","IMPRINT",FACE,{"disambiguationData":[TD([[makeQuery(id+"F10.imprint","IMPRINT",EDGE,{"derivedFrom":sQuery(id+"F10.wireOp",EDGE,"E96")}),1.0]])]});
            var Q2;
            Q2=makeQuery(id+"F13.opExtrude","CAP_EDGE",EDGE,{"disambiguationData":[OSD([sQuery(id+"F0.wireOp",EDGE,"E3.0")]),OD(0.0)],"isStart":false});
            sweep(context, id + "F14", {"operationType" : NewBodyOperationType.REMOVE, "profiles" : qUnion([Q0, Q1]), "path" : qUnion([Q2])});
        }
        {
            var Q0;
            Q0=makeQuery(id+"F12.imprint","IMPRINT",FACE,{"disambiguationData":[TD([[makeQuery(id+"F12.imprint","IMPRINT",EDGE,{"derivedFrom":sQuery(id+"F12.wireOp",EDGE,"E107")}),1.0]])]});
            var Q1;
            Q1=makeQuery(id+"F10.imprint","IMPRINT",FACE,{"disambiguationData":[TD([[makeQuery(id+"F10.imprint","IMPRINT",EDGE,{"derivedFrom":sQuery(id+"F10.wireOp",EDGE,"E92")}),1.0]])]});
            var Q2;
            Q2=makeQuery(id+"F13.opExtrude","CAP_EDGE",EDGE,{"disambiguationData":[OSD([sQuery(id+"F0.wireOp",EDGE,"E3.0")]),OD(4.0)],"isStart":false});
            sweep(context, id + "F15", {"operationType" : NewBodyOperationType.REMOVE, "profiles" : qUnion([Q0, Q1]), "path" : qUnion([Q2])});
        }
        {
            var Q0;
            Q0=makeQuery(id+"F10.imprint","IMPRINT",FACE,{"disambiguationData":[TD([[makeQuery(id+"F10.imprint","IMPRINT",EDGE,{"derivedFrom":sQuery(id+"F10.wireOp",EDGE,"E93")}),1.0]])]});
            var Q1;
            Q1=makeQuery(id+"F12.imprint","IMPRINT",FACE,{"disambiguationData":[TD([[makeQuery(id+"F12.imprint","IMPRINT",EDGE,{"derivedFrom":sQuery(id+"F12.wireOp",EDGE,"E106")}),1.0]])]});
            var Q2;
            Q2=makeQuery(id+"F13.opExtrude","CAP_EDGE",EDGE,{"disambiguationData":[OSD([sQuery(id+"F0.wireOp",EDGE,"E3.0")]),OD(3.0)],"isStart":false});
            sweep(context, id + "F16", {"operationType" : NewBodyOperationType.REMOVE, "profiles" : qUnion([Q0, Q1]), "path" : qUnion([Q2])});
        }
        {
            var Q0;
            Q0=makeQuery(id+"F12.imprint","IMPRINT",FACE,{"disambiguationData":[TD([[makeQuery(id+"F12.imprint","IMPRINT",EDGE,{"derivedFrom":sQuery(id+"F12.wireOp",EDGE,"E105")}),1.0]])]});
            var Q1;
            Q1=makeQuery(id+"F10.imprint","IMPRINT",FACE,{"disambiguationData":[TD([[makeQuery(id+"F10.imprint","IMPRINT",EDGE,{"derivedFrom":sQuery(id+"F10.wireOp",EDGE,"E94")}),1.0]])]});
            var Q2;
            Q2=makeQuery(id+"F13.opExtrude","CAP_EDGE",EDGE,{"disambiguationData":[OSD([sQuery(id+"F0.wireOp",EDGE,"E3.0")]),OD(2.0)],"isStart":false});
            sweep(context, id + "F17", {"operationType" : NewBodyOperationType.REMOVE, "profiles" : qUnion([Q0, Q1]), "path" : qUnion([Q2])});
        }
        {
            var Q0;
            Q0=makeQuery(id+"F13.opExtrude","SWEPT_EDGE",EDGE,{"disambiguationData":[OSD([sQuery(id+"F9.wireOp",VERTEX,"E77.start")])]});
            cPlane(context, id + "F18", {"entities" : qUnion([Q0]), "cplaneType" : CPlaneType.LINE_ANGLE, "offset" : 25.4 * mm, "angle" : 90 * degree, "width" : 152.4 * mm, "height" : 152.4 * mm});
        }
        {
            var Q0;
            Q0=qCreatedBy(id+"F18.planeOp",FACE);
            var sketch = newSketch(context, id + "F19", { "sketchPlane" : qUnion([Q0])});
            skPoint(sketch, "E108.0", {"position": v(-38.66, 14.4) * mm});
            skCircle(sketch, "E109", {"center": v(-38.66, 14.4) * mm, "radius": 1.27 * mm});
            skSolve(sketch);
        }
        {
            var Q0;
            Q0=makeQuery(id+"F19.imprint","IMPRINT",FACE,{"disambiguationData":[TD([[makeQuery(id+"F19.imprint","IMPRINT",EDGE,{"derivedFrom":sQuery(id+"F19.wireOp",EDGE,"E109")}),1.0]])]});
            var Q1;
            Q1=makeQuery(id+"F10.imprint","IMPRINT",FACE,{"disambiguationData":[TD([[makeQuery(id+"F10.imprint","IMPRINT",EDGE,{"derivedFrom":sQuery(id+"F10.wireOp",EDGE,"E95")}),1.0]])]});
            var Q2;
            Q2=makeQuery(id+"F13.opExtrude","CAP_EDGE",EDGE,{"disambiguationData":[OSD([sQuery(id+"F0.wireOp",EDGE,"E3.0")]),OD(1.0)],"isStart":false});
            sweep(context, id + "F20", {"operationType" : NewBodyOperationType.REMOVE, "profiles" : qUnion([Q0, Q1]), "path" : qUnion([Q2])});
        }
        {
            var Q0;
            Q0=makeQuery(id+"F13.opExtrude","SWEPT_BODY",BODY,{"disambiguationData":[OSD([sQuery(id+"F9.wireOp",EDGE,"E76")])]});
            var Q1;
            Q1=makeQuery(id+"F13.opExtrude","SWEPT_BODY",BODY,{"disambiguationData":[OSD([sQuery(id+"F9.wireOp",EDGE,"E77")])]});
            var Q2;
            Q2=makeQuery(id+"F13.opExtrude","SWEPT_BODY",BODY,{"disambiguationData":[OSD([sQuery(id+"F9.wireOp",EDGE,"E78")])]});
            var Q3;
            Q3=makeQuery(id+"F13.opExtrude","SWEPT_BODY",BODY,{"disambiguationData":[OSD([sQuery(id+"F9.wireOp",EDGE,"E79")])]});
            var Q4;
            Q4=makeQuery(id+"F13.opExtrude","SWEPT_BODY",BODY,{"disambiguationData":[OSD([sQuery(id+"F9.wireOp",EDGE,"E80")])]});
            deleteBodies(context, id + "F21", {"entities" : qUnion([Q0, Q1, Q2, Q3, Q4])});
        }
        {
            var Q0;
            Q0=makeQuery(id+"F20.boolean.opBoolean","COPY",FACE,{"derivedFrom":makeQuery(id+"F20.opSweep","CAP_FACE",FACE,{"disambiguationData":[OSD([sQuery(id+"F9.wireOp",EDGE,"E77"),sQuery(id+"F19.wireOp",EDGE,"E109")])],"isStart":true})});
            extrude(context, id + "F22", {"entities" : qUnion([Q0]), "operationType" : NewBodyOperationType.REMOVE, "endBound" : BoundingType.THROUGH_ALL, "oppositeDirection" : true, "depth" : 25.4 * mm, "offsetDistance" : 25.4 * mm});
        }
        {
            var Q0;
            Q0=makeQuery(id+"F20.boolean.opBoolean","COPY",FACE,{"derivedFrom":makeQuery(id+"F20.opSweep","CAP_FACE",FACE,{"disambiguationData":[OSD([sQuery(id+"F9.wireOp",EDGE,"E77"),sQuery(id+"F10.wireOp",EDGE,"E95")])],"isStart":false})});
            var sketch = newSketch(context, id + "F23", { "sketchPlane" : qUnion([Q0])});
            skFitSpline(sketch, "E110.0", {"points": [v(25.07, 14.81) * mm, v(24.92, 14.84) * mm, v(24.63, 14.95) * mm, v(24.28, 15.27) * mm, v(24.08, 15.71) * mm, v(24.05, 16.2) * mm, v(24.2, 16.68) * mm, v(24.49, 17.06) * mm, v(24.9, 17.3) * mm, v(25.2, 17.34) * mm, v(25.36, 17.33) * mm]});
            skCircle(sketch, "E111", {"center": v(25.24, 16.07) * mm, "radius": 1.27 * mm});
            skSolve(sketch);
        }
        {
            var Q0;
            Q0=qSketchRegion(id+"F23",true);
            extrude(context, id + "F24", {"entities" : qUnion([Q0]), "operationType" : NewBodyOperationType.REMOVE, "endBound" : BoundingType.THROUGH_ALL, "oppositeDirection" : true, "depth" : 25.4 * mm, "offsetDistance" : 25.4 * mm});
        }
        {
            var Q0;
            {var subQ0=sQuery(id+"F5.wireOp",EDGE,"E26.0.3");var subQ1=makeQuery(id+"F5.imprint","INTERSECT",VERTEX,{"derivedFrom":[subQ0,sQuery(id+"F5.wireOp",EDGE,"E36")]});var subQ2=makeQuery(id+"F5.imprint","INTERSECT",VERTEX,{"derivedFrom":[subQ0,sQuery(id+"F5.wireOp",EDGE,"E37")]});var subQ3=makeQuery(id+"F5.imprint","INTERSECT",VERTEX,{"derivedFrom":[subQ0,sQuery(id+"F5.wireOp",EDGE,"E38")]});var subQ4=makeQuery(id+"F5.imprint","INTERSECT",VERTEX,{"derivedFrom":[subQ0,sQuery(id+"F5.wireOp",EDGE,"E39")]});var subQ5=makeQuery(id+"F5.imprint","INTERSECT",VERTEX,{"derivedFrom":[subQ0,sQuery(id+"F5.wireOp",EDGE,"E40")]});Q0=makeQuery(id+"F6.boolean.opBoolean","MERGE",FACE,{"derivedFrom":[makeQuery(id+"F1.opExtrude","CAP_FACE",FACE,{"disambiguationData":[OSD([sQuery(id+"F0.wireOp",EDGE,"E2"),sQuery(id+"F0.wireOp",EDGE,"E3.0"),sQuery(id+"F0.wireOp",EDGE,"E4"),sQuery(id+"F0.wireOp",EDGE,"E5")])],"isStart":true}),makeQuery(id+"F6.opExtrude","SWEPT_FACE",FACE,{"disambiguationData":[OSD([subQ0]),TDD([makeQuery(id+"F5.imprint","IMPRINT",EDGE,{"disambiguationData":[TD([[subQ5,1.0]])],"derivedFrom":subQ0}),makeQuery(id+"F5.imprint","IMPRINT",EDGE,{"disambiguationData":[TD([[subQ5,-1.0]])],"derivedFrom":subQ0})])]}),makeQuery(id+"F6.opExtrude","SWEPT_FACE",FACE,{"disambiguationData":[OSD([subQ0]),TDD([makeQuery(id+"F5.imprint","IMPRINT",EDGE,{"disambiguationData":[TD([[subQ4,1.0]])],"derivedFrom":subQ0}),makeQuery(id+"F5.imprint","IMPRINT",EDGE,{"disambiguationData":[TD([[subQ4,-1.0]])],"derivedFrom":subQ0})])]}),makeQuery(id+"F6.opExtrude","SWEPT_FACE",FACE,{"disambiguationData":[OSD([subQ0]),TDD([makeQuery(id+"F5.imprint","IMPRINT",EDGE,{"disambiguationData":[TD([[subQ3,1.0]])],"derivedFrom":subQ0}),makeQuery(id+"F5.imprint","IMPRINT",EDGE,{"disambiguationData":[TD([[subQ3,-1.0]])],"derivedFrom":subQ0})])]}),makeQuery(id+"F6.opExtrude","SWEPT_FACE",FACE,{"disambiguationData":[OSD([subQ0]),TDD([makeQuery(id+"F5.imprint","IMPRINT",EDGE,{"disambiguationData":[TD([[subQ2,1.0]])],"derivedFrom":subQ0}),makeQuery(id+"F5.imprint","IMPRINT",EDGE,{"disambiguationData":[TD([[subQ2,-1.0]])],"derivedFrom":subQ0})])]}),makeQuery(id+"F6.opExtrude","SWEPT_FACE",FACE,{"disambiguationData":[OSD([subQ0]),TDD([makeQuery(id+"F5.imprint","IMPRINT",EDGE,{"disambiguationData":[TD([[subQ1,1.0]])],"derivedFrom":subQ0}),makeQuery(id+"F5.imprint","IMPRINT",EDGE,{"disambiguationData":[TD([[subQ1,-1.0]])],"derivedFrom":subQ0})])]})]});}
            cPlane(context, id + "F25", {"entities" : qUnion([Q0]), "cplaneType" : CPlaneType.OFFSET, "offset" : 12.7 * mm, "width" : 152.4 * mm, "height" : 152.4 * mm});
        }
        {
            var Q0;
            Q0=qCreatedBy(id+"F25.planeOp",FACE);
            var sketch = newSketch(context, id + "F26", { "sketchPlane" : qUnion([Q0])});
            skLineSegment(sketch, "E112.0.20", {"start": v(11.94, 9.45) * mm, "end": v(11.94, 7.5) * mm});
            skArc(sketch, "E112.0.21", {"start": v(11.94, 7.5) * mm, "mid": v(36.13, 12.7) * mm, "end": v(60.2, 6.95) * mm});
            skLineSegment(sketch, "E112.0.22", {"start": v(60.2, 6.95) * mm, "end": v(60.2, 8.93) * mm});
            skArc(sketch, "E113", {"start": v(60.2, 8.93) * mm, "mid": v(36.13, 14.47) * mm, "end": v(11.94, 9.45) * mm});
            skCircle(sketch, "E114", {"center": v(29.72, 14.19) * mm, "radius": 1.27 * mm});
            skCircle(sketch, "E115", {"center": v(50.04, 12.62) * mm, "radius": 1.27 * mm});
            skCircle(sketch, "E116", {"center": v(44.96, 13.7) * mm, "radius": 1.27 * mm});
            skCircle(sketch, "E117", {"center": v(39.88, 14.31) * mm, "radius": 1.27 * mm});
            skCircle(sketch, "E118", {"center": v(34.8, 14.47) * mm, "radius": 1.27 * mm});
            skSolve(sketch);
        }
        {
            var Q0;
            {var subQ0=sQuery(id+"F5.wireOp",EDGE,"E26.0.3");var subQ1=makeQuery(id+"F5.imprint","INTERSECT",VERTEX,{"derivedFrom":[subQ0,sQuery(id+"F5.wireOp",EDGE,"E36")]});var subQ2=makeQuery(id+"F5.imprint","INTERSECT",VERTEX,{"derivedFrom":[subQ0,sQuery(id+"F5.wireOp",EDGE,"E37")]});var subQ3=makeQuery(id+"F5.imprint","INTERSECT",VERTEX,{"derivedFrom":[subQ0,sQuery(id+"F5.wireOp",EDGE,"E38")]});var subQ4=makeQuery(id+"F5.imprint","INTERSECT",VERTEX,{"derivedFrom":[subQ0,sQuery(id+"F5.wireOp",EDGE,"E39")]});var subQ5=makeQuery(id+"F5.imprint","INTERSECT",VERTEX,{"derivedFrom":[subQ0,sQuery(id+"F5.wireOp",EDGE,"E40")]});Q0=makeQuery(id+"F6.boolean.opBoolean","MERGE",FACE,{"derivedFrom":[makeQuery(id+"F1.opExtrude","CAP_FACE",FACE,{"disambiguationData":[OSD([sQuery(id+"F0.wireOp",EDGE,"E2"),sQuery(id+"F0.wireOp",EDGE,"E3.0"),sQuery(id+"F0.wireOp",EDGE,"E4"),sQuery(id+"F0.wireOp",EDGE,"E5")])],"isStart":true}),makeQuery(id+"F6.opExtrude","SWEPT_FACE",FACE,{"disambiguationData":[OSD([subQ0]),TDD([makeQuery(id+"F5.imprint","IMPRINT",EDGE,{"disambiguationData":[TD([[subQ5,1.0]])],"derivedFrom":subQ0}),makeQuery(id+"F5.imprint","IMPRINT",EDGE,{"disambiguationData":[TD([[subQ5,-1.0]])],"derivedFrom":subQ0})])]}),makeQuery(id+"F6.opExtrude","SWEPT_FACE",FACE,{"disambiguationData":[OSD([subQ0]),TDD([makeQuery(id+"F5.imprint","IMPRINT",EDGE,{"disambiguationData":[TD([[subQ4,1.0]])],"derivedFrom":subQ0}),makeQuery(id+"F5.imprint","IMPRINT",EDGE,{"disambiguationData":[TD([[subQ4,-1.0]])],"derivedFrom":subQ0})])]}),makeQuery(id+"F6.opExtrude","SWEPT_FACE",FACE,{"disambiguationData":[OSD([subQ0]),TDD([makeQuery(id+"F5.imprint","IMPRINT",EDGE,{"disambiguationData":[TD([[subQ3,1.0]])],"derivedFrom":subQ0}),makeQuery(id+"F5.imprint","IMPRINT",EDGE,{"disambiguationData":[TD([[subQ3,-1.0]])],"derivedFrom":subQ0})])]}),makeQuery(id+"F6.opExtrude","SWEPT_FACE",FACE,{"disambiguationData":[OSD([subQ0]),TDD([makeQuery(id+"F5.imprint","IMPRINT",EDGE,{"disambiguationData":[TD([[subQ2,1.0]])],"derivedFrom":subQ0}),makeQuery(id+"F5.imprint","IMPRINT",EDGE,{"disambiguationData":[TD([[subQ2,-1.0]])],"derivedFrom":subQ0})])]}),makeQuery(id+"F6.opExtrude","SWEPT_FACE",FACE,{"disambiguationData":[OSD([subQ0]),TDD([makeQuery(id+"F5.imprint","IMPRINT",EDGE,{"disambiguationData":[TD([[subQ1,1.0]])],"derivedFrom":subQ0}),makeQuery(id+"F5.imprint","IMPRINT",EDGE,{"disambiguationData":[TD([[subQ1,-1.0]])],"derivedFrom":subQ0})])]})]});}
            var sketch = newSketch(context, id + "F27", { "sketchPlane" : qUnion([Q0])});
            skLineSegment(sketch, "E119.0.20", {"start": v(11.94, 9.45) * mm, "end": v(11.94, 7.5) * mm});
            skArc(sketch, "E119.0.21", {"start": v(11.94, 7.5) * mm, "mid": v(36.13, 12.7) * mm, "end": v(60.2, 6.95) * mm});
            skLineSegment(sketch, "E119.0.22", {"start": v(60.2, 6.95) * mm, "end": v(60.2, 8.93) * mm});
            skArc(sketch, "E120", {"start": v(60.2, 8.93) * mm, "mid": v(36.13, 14.47) * mm, "end": v(11.94, 9.45) * mm});
            skCircle(sketch, "E121", {"center": v(27.9, 13.98) * mm, "radius": 1.27 * mm});
            skCircle(sketch, "E122", {"center": v(36, 14.48) * mm, "radius": 1.27 * mm});
            skCircle(sketch, "E123", {"center": v(19.79, 12.3) * mm, "radius": 1.27 * mm});
            skCircle(sketch, "E124", {"center": v(44.13, 13.83) * mm, "radius": 1.27 * mm});
            skCircle(sketch, "E125", {"center": v(52.32, 11.97) * mm, "radius": 1.27 * mm});
            skSolve(sketch);
        }
        {
            var Q0;
            {var subQ41=sQuery(id+"F27.wireOp",EDGE,"E119.0.20");Q0=makeQuery(id+"F27.imprint","IMPRINT",FACE,{"disambiguationData":[TD([[makeQuery(id+"F27.imprint","IMPRINT",EDGE,{"derivedFrom":subQ41}),-1.0]])]});}
            var Q1;
            {var subQ0=sQuery(id+"F27.wireOp",EDGE,"E123");var subQ1=sQuery(id+"F27.wireOp",EDGE,"E120");var subQ2=makeQuery(id+"F27.imprint","INTERSECT",VERTEX,{"disambiguationData":[OD(1.0)],"derivedFrom":[subQ1,subQ0]});Q1=makeQuery(id+"F27.imprint","IMPRINT",FACE,{"disambiguationData":[TD([[makeQuery(id+"F27.imprint","IMPRINT",EDGE,{"disambiguationData":[TD([[subQ2,-1.0]])],"derivedFrom":subQ1}),1.0]])]});}
            var Q2;
            {var subQ1=sQuery(id+"F0.wireOp",EDGE,"E3.0");var subQ2=sQuery(id+"F5.wireOp",EDGE,"E26.0.3");var subQ3=makeQuery(id+"F5.imprint","INTERSECT",VERTEX,{"derivedFrom":[subQ2,sQuery(id+"F5.wireOp",EDGE,"E36")]});var subQ4=makeQuery(id+"F5.imprint","INTERSECT",VERTEX,{"derivedFrom":[subQ2,sQuery(id+"F5.wireOp",EDGE,"E37")]});var subQ5=makeQuery(id+"F5.imprint","INTERSECT",VERTEX,{"derivedFrom":[subQ2,sQuery(id+"F5.wireOp",EDGE,"E38")]});var subQ6=makeQuery(id+"F5.imprint","INTERSECT",VERTEX,{"derivedFrom":[subQ2,sQuery(id+"F5.wireOp",EDGE,"E39")]});var subQ7=makeQuery(id+"F5.imprint","INTERSECT",VERTEX,{"derivedFrom":[subQ2,sQuery(id+"F5.wireOp",EDGE,"E40")]});var subQ8=makeQuery(id+"F16.boolean.opBoolean","INTERSECT",EDGE,{"derivedFrom":[makeQuery(id+"F6.boolean.opBoolean","MERGE",FACE,{"derivedFrom":[makeQuery(id+"F1.opExtrude","CAP_FACE",FACE,{"disambiguationData":[OSD([sQuery(id+"F0.wireOp",EDGE,"E2"),subQ1,sQuery(id+"F0.wireOp",EDGE,"E4"),sQuery(id+"F0.wireOp",EDGE,"E5")])],"isStart":true}),makeQuery(id+"F6.opExtrude","SWEPT_FACE",FACE,{"disambiguationData":[OSD([subQ2]),TDD([makeQuery(id+"F5.imprint","IMPRINT",EDGE,{"disambiguationData":[TD([[subQ7,1.0]])],"derivedFrom":subQ2}),makeQuery(id+"F5.imprint","IMPRINT",EDGE,{"disambiguationData":[TD([[subQ7,-1.0]])],"derivedFrom":subQ2})])]}),makeQuery(id+"F6.opExtrude","SWEPT_FACE",FACE,{"disambiguationData":[OSD([subQ2]),TDD([makeQuery(id+"F5.imprint","IMPRINT",EDGE,{"disambiguationData":[TD([[subQ6,1.0]])],"derivedFrom":subQ2}),makeQuery(id+"F5.imprint","IMPRINT",EDGE,{"disambiguationData":[TD([[subQ6,-1.0]])],"derivedFrom":subQ2})])]}),makeQuery(id+"F6.opExtrude","SWEPT_FACE",FACE,{"disambiguationData":[OSD([subQ2]),TDD([makeQuery(id+"F5.imprint","IMPRINT",EDGE,{"disambiguationData":[TD([[subQ5,1.0]])],"derivedFrom":subQ2}),makeQuery(id+"F5.imprint","IMPRINT",EDGE,{"disambiguationData":[TD([[subQ5,-1.0]])],"derivedFrom":subQ2})])]}),makeQuery(id+"F6.opExtrude","SWEPT_FACE",FACE,{"disambiguationData":[OSD([subQ2]),TDD([makeQuery(id+"F5.imprint","IMPRINT",EDGE,{"disambiguationData":[TD([[subQ4,1.0]])],"derivedFrom":subQ2}),makeQuery(id+"F5.imprint","IMPRINT",EDGE,{"disambiguationData":[TD([[subQ4,-1.0]])],"derivedFrom":subQ2})])]}),makeQuery(id+"F6.opExtrude","SWEPT_FACE",FACE,{"disambiguationData":[OSD([subQ2]),TDD([makeQuery(id+"F5.imprint","IMPRINT",EDGE,{"disambiguationData":[TD([[subQ3,1.0]])],"derivedFrom":subQ2}),makeQuery(id+"F5.imprint","IMPRINT",EDGE,{"disambiguationData":[TD([[subQ3,-1.0]])],"derivedFrom":subQ2})])]})]}),makeQuery(id+"F16.opSweep","SWEPT_FACE",FACE,{"disambiguationData":[OSD([subQ1,sQuery(id+"F12.wireOp",EDGE,"E106")])]})]});Q2=makeQuery(id+"F27.imprint","IMPRINT",FACE,{"disambiguationData":[TD([[makeQuery(id+"F27.imprint","IMPRINT",EDGE,{"derivedFrom":subQ8}),1.0]])]});}
            extrude(context, id + "F28", {"entities" : qUnion([Q0, Q1, Q2]), "operationType" : NewBodyOperationType.ADD, "depth" : 0.25 * mm, "offsetDistance" : 25.4 * mm});
        }
        {
            var Q1;
            Q1=makeQuery(id+"F28.opExtrude","CAP_FACE",FACE,{"disambiguationData":[OSD([sQuery(id+"F27.wireOp",EDGE,"E119.0.20"),sQuery(id+"F27.wireOp",EDGE,"E119.0.21"),sQuery(id+"F27.wireOp",EDGE,"E119.0.22"),sQuery(id+"F27.wireOp",EDGE,"E120"),sQuery(id+"F27.wireOp",EDGE,"E121"),sQuery(id+"F27.wireOp",EDGE,"E122"),sQuery(id+"F27.wireOp",EDGE,"E123"),sQuery(id+"F27.wireOp",EDGE,"E124"),sQuery(id+"F27.wireOp",EDGE,"E125")])],"isStart":false});
            var Q2;
            {var subQ15=sQuery(id+"F26.wireOp",EDGE,"E112.0.20");Q2=makeQuery(id+"F26.imprint","IMPRINT",FACE,{"disambiguationData":[TD([[makeQuery(id+"F26.imprint","IMPRINT",EDGE,{"derivedFrom":subQ15}),1.0]])]});}
            loft(context, id + "F29", {"operationType" : NewBodyOperationType.ADD, "sheetProfilesArray" : [{ "sheetProfileEntities" : qUnion([Q1]) }, { "sheetProfileEntities" : qUnion([Q2]) }]});
        }
        {
            var Q0;
            Q0=qCreatedBy(id+"F2.planeOp",FACE);
            cPlane(context, id + "F30", {"entities" : qUnion([Q0]), "cplaneType" : CPlaneType.OFFSET, "offset" : 10.16 * mm, "oppositeDirection" : true, "width" : 152.4 * mm, "height" : 152.4 * mm});
        }
        {
            var Q0;
            Q0=qCreatedBy(id+"F30.planeOp",FACE);
            var sketch = newSketch(context, id + "F31", { "sketchPlane" : qUnion([Q0])});
            skPoint(sketch, "E126.0", {"position": v(11.94, -12.7) * mm});
            skFitSpline(sketch, "E127.0", {"points": [v(17.02, -11.29) * mm, v(15.95, -10.67) * mm, v(14.9, -10.06) * mm, v(13.84, -9.45) * mm]});
            skFitSpline(sketch, "E128.0", {"points": [v(13.84, -9.45) * mm, v(13.84, -8.23) * mm, v(13.84, -7) * mm, v(13.84, -5.79) * mm]});
            skFitSpline(sketch, "E129.0", {"points": [v(13.84, -5.79) * mm, v(14.9, -5.18) * mm, v(15.95, -4.57) * mm, v(17.02, -3.95) * mm]});
            skFitSpline(sketch, "E130.0", {"points": [v(17.02, -3.95) * mm, v(18.07, -4.56) * mm, v(19.13, -5.17) * mm, v(20.2, -5.79) * mm]});
            skFitSpline(sketch, "E131.0", {"points": [v(20.2, -5.79) * mm, v(20.2, -7) * mm, v(20.2, -8.23) * mm, v(20.2, -9.45) * mm]});
            skFitSpline(sketch, "E132.0", {"points": [v(20.2, -9.45) * mm, v(19.13, -10.07) * mm, v(18.07, -10.68) * mm, v(17.02, -11.29) * mm]});
            skFitSpline(sketch, "E133.0", {"points": [v(56.39, -11.92) * mm, v(55.34, -11.32) * mm, v(54.28, -10.7) * mm, v(53.21, -10.09) * mm]});
            skFitSpline(sketch, "E134.0", {"points": [v(53.21, -10.09) * mm, v(53.21, -8.87) * mm, v(53.21, -7.64) * mm, v(53.21, -6.42) * mm]});
            skFitSpline(sketch, "E135.0", {"points": [v(53.21, -6.42) * mm, v(54.28, -5.8) * mm, v(55.34, -5.2) * mm, v(56.39, -4.59) * mm]});
            skFitSpline(sketch, "E136.0", {"points": [v(56.39, -4.59) * mm, v(57.46, -5.2) * mm, v(58.52, -5.82) * mm, v(59.56, -6.42) * mm]});
            skFitSpline(sketch, "E137.0", {"points": [v(59.56, -6.42) * mm, v(59.56, -7.64) * mm, v(59.56, -8.87) * mm, v(59.56, -10.09) * mm]});
            skLineSegment(sketch, "E138", {"start": v(13.84, -5.79) * mm, "end": v(20.2, -9.45) * mm});
            skLineSegment(sketch, "E139", {"start": v(53.21, -6.42) * mm, "end": v(59.56, -10.09) * mm});
            skFitSpline(sketch, "E140.0", {"points": [v(59.56, -10.09) * mm, v(58.52, -10.7) * mm, v(57.46, -11.3) * mm, v(56.39, -11.92) * mm]});
            skCircle(sketch, "E141.cCircle", {"center": v(17.02, -7.62) * mm, "radius": 4.45 * mm, "construction": true});
            skLineSegment(sketch, "E141.0", {"start": v(21.46, -5.05) * mm, "end": v(21.46, -10.19) * mm});
            skLineSegment(sketch, "E141.1", {"start": v(21.46, -10.19) * mm, "end": v(17.02, -12.75) * mm});
            skLineSegment(sketch, "E141.2", {"start": v(17.02, -12.75) * mm, "end": v(12.57, -10.19) * mm});
            skLineSegment(sketch, "E141.3", {"start": v(12.57, -10.19) * mm, "end": v(12.57, -5.05) * mm});
            skLineSegment(sketch, "E141.4", {"start": v(12.57, -5.05) * mm, "end": v(17.02, -2.49) * mm});
            skLineSegment(sketch, "E141.5", {"start": v(17.02, -2.49) * mm, "end": v(21.46, -5.05) * mm});
            skPoint(sketch, "E141.0.midPoint", {"position": v(21.46, -7.62) * mm});
            skCircle(sketch, "E142.cCircle", {"center": v(56.39, -8.26) * mm, "radius": 4.44 * mm, "construction": true});
            skLineSegment(sketch, "E142.0", {"start": v(60.83, -5.69) * mm, "end": v(60.83, -10.82) * mm});
            skLineSegment(sketch, "E142.1", {"start": v(60.83, -10.82) * mm, "end": v(56.39, -13.39) * mm});
            skLineSegment(sketch, "E142.2", {"start": v(56.39, -13.39) * mm, "end": v(51.94, -10.82) * mm});
            skLineSegment(sketch, "E142.3", {"start": v(51.94, -10.82) * mm, "end": v(51.94, -5.69) * mm});
            skLineSegment(sketch, "E142.4", {"start": v(51.94, -5.69) * mm, "end": v(56.39, -3.12) * mm});
            skLineSegment(sketch, "E142.5", {"start": v(56.39, -3.12) * mm, "end": v(60.83, -5.69) * mm});
            skPoint(sketch, "E142.0.midPoint", {"position": v(60.83, -8.26) * mm});
            skLineSegment(sketch, "E143", {"start": v(53.21, -6.42) * mm, "end": v(53.21, -4.96) * mm});
            skLineSegment(sketch, "E144", {"start": v(53.21, -10.09) * mm, "end": v(53.21, -11.55) * mm});
            skFitSpline(sketch, "E145.0", {"points": [v(28.46, -12.7) * mm, v(22.95, -12.7) * mm, v(17.44, -12.7) * mm, v(11.94, -12.7) * mm]});
            skFitSpline(sketch, "E146.0", {"points": [v(60.2, -12.7) * mm, v(57.22, -12.7) * mm, v(54.24, -12.7) * mm, v(51.26, -12.7) * mm]});
            skFitSpline(sketch, "E147.0", {"points": [v(60.2, -0.25) * mm, v(60.2, -4.4) * mm, v(60.2, -8.55) * mm, v(60.2, -12.7) * mm]});
            skFitSpline(sketch, "E148.0.0", {"points": [v(11.94, -0.25) * mm, v(11.94, -4.4) * mm, v(11.94, -8.55) * mm, v(11.94, -12.7) * mm]});
            skFitSpline(sketch, "E148.0.1", {"points": [v(11.94, -12.7) * mm, v(17.44, -12.7) * mm, v(22.95, -12.7) * mm, v(28.46, -12.7) * mm]});
            skFitSpline(sketch, "E148.0.2", {"points": [v(28.46, -12.7) * mm, v(25.16, -8.55) * mm, v(21.86, -4.4) * mm, v(18.57, -0.25) * mm]});
            skLineSegment(sketch, "E148.0.3", {"start": v(18.57, -0.25) * mm, "end": v(11.94, -0.25) * mm});
            skFitSpline(sketch, "E149.0.0", {"points": [v(53.53, -0.25) * mm, v(52.78, -4.4) * mm, v(52.02, -8.55) * mm, v(51.26, -12.7) * mm]});
            skFitSpline(sketch, "E149.0.1", {"points": [v(51.26, -12.7) * mm, v(54.24, -12.7) * mm, v(57.22, -12.7) * mm, v(60.2, -12.7) * mm]});
            skFitSpline(sketch, "E149.0.2", {"points": [v(60.2, -12.7) * mm, v(60.2, -8.55) * mm, v(60.2, -4.4) * mm, v(60.2, -0.25) * mm]});
            skFitSpline(sketch, "E149.0.3", {"points": [v(60.2, -0.25) * mm, v(57.98, -0.25) * mm, v(55.75, -0.25) * mm, v(53.53, -0.25) * mm]});
            skFitSpline(sketch, "E150.0.0", {"points": [v(21.01, -0.25) * mm, v(24.34, -4.4) * mm, v(27.66, -8.55) * mm, v(30.98, -12.7) * mm]});
            skLineSegment(sketch, "E150.0.1", {"start": v(30.98, -12.7) * mm, "end": v(33.53, -12.7) * mm});
            skFitSpline(sketch, "E150.0.2", {"points": [v(33.53, -12.7) * mm, v(31.23, -8.55) * mm, v(28.94, -4.4) * mm, v(26.64, -0.25) * mm]});
            skFitSpline(sketch, "E150.0.3", {"points": [v(26.64, -0.25) * mm, v(24.77, -0.25) * mm, v(22.89, -0.25) * mm, v(21.01, -0.25) * mm]});
            skFitSpline(sketch, "E151.0.0", {"points": [v(29.16, -0.25) * mm, v(31.46, -4.4) * mm, v(33.77, -8.55) * mm, v(36.07, -12.7) * mm]});
            skLineSegment(sketch, "E151.0.1", {"start": v(36.07, -12.7) * mm, "end": v(38.61, -12.7) * mm});
            skFitSpline(sketch, "E151.0.2", {"points": [v(38.61, -12.7) * mm, v(37.31, -8.55) * mm, v(36.02, -4.4) * mm, v(34.72, -0.25) * mm]});
            skFitSpline(sketch, "E151.0.3", {"points": [v(34.72, -0.25) * mm, v(32.87, -0.25) * mm, v(31.02, -0.25) * mm, v(29.16, -0.25) * mm]});
            skFitSpline(sketch, "E152.0.0", {"points": [v(37.26, -0.25) * mm, v(38.56, -4.4) * mm, v(39.85, -8.55) * mm, v(41.14, -12.7) * mm]});
            skLineSegment(sketch, "E152.0.1", {"start": v(41.14, -12.7) * mm, "end": v(43.7, -12.7) * mm});
            skFitSpline(sketch, "E152.0.2", {"points": [v(43.7, -12.7) * mm, v(43.43, -8.55) * mm, v(43.15, -4.4) * mm, v(42.88, -0.25) * mm]});
            skFitSpline(sketch, "E152.0.3", {"points": [v(42.88, -0.25) * mm, v(41, -0.25) * mm, v(39.13, -0.25) * mm, v(37.26, -0.25) * mm]});
            skFitSpline(sketch, "E153.0.0", {"points": [v(45.39, -0.25) * mm, v(45.66, -4.4) * mm, v(45.93, -8.55) * mm, v(46.2, -12.7) * mm]});
            skLineSegment(sketch, "E153.0.1", {"start": v(46.2, -12.7) * mm, "end": v(48.8, -12.7) * mm});
            skFitSpline(sketch, "E153.0.2", {"points": [v(48.8, -12.7) * mm, v(49.57, -8.55) * mm, v(50.34, -4.4) * mm, v(51.1, -0.25) * mm]});
            skFitSpline(sketch, "E153.0.3", {"points": [v(51.1, -0.25) * mm, v(49.2, -0.25) * mm, v(47.3, -0.25) * mm, v(45.39, -0.25) * mm]});
            skSolve(sketch);
        }
        {
            var Q0;
            Q0=makeQuery(id+"F31.imprint","IMPRINT",FACE,{"disambiguationData":[TD([[makeQuery(id+"F31.imprint","IMPRINT",EDGE,{"derivedFrom":sQuery(id+"F31.wireOp",EDGE,"E129.0")}),-1.0]])]});
            var Q1;
            Q1=makeQuery(id+"F31.imprint","IMPRINT",FACE,{"disambiguationData":[TD([[makeQuery(id+"F31.imprint","IMPRINT",EDGE,{"derivedFrom":sQuery(id+"F31.wireOp",EDGE,"E127.0")}),-1.0]])]});
            var Q2;
            Q2=makeQuery(id+"F31.imprint","IMPRINT",FACE,{"disambiguationData":[TD([[makeQuery(id+"F31.imprint","IMPRINT",EDGE,{"derivedFrom":sQuery(id+"F31.wireOp",EDGE,"E127.0")}),1.0]])]});
            var Q3;
            {var subQ5=sQuery(id+"F31.wireOp",EDGE,"E141.0");Q3=makeQuery(id+"F31.imprint","IMPRINT",FACE,{"disambiguationData":[TD([[makeQuery(id+"F31.imprint","IMPRINT",EDGE,{"derivedFrom":subQ5}),1.0]])]});}
            var Q4;
            Q4=makeQuery(id+"F29.opLoft","SWEPT_FACE",FACE,{"disambiguationData":[OSD([sQuery(id+"F26.wireOp",EDGE,"E112.0.20"),sQuery(id+"F26.wireOp",EDGE,"E113"),sQuery(id+"F26.wireOp",EDGE,"E114"),sQuery(id+"F27.wireOp",EDGE,"E119.0.20"),sQuery(id+"F27.wireOp",EDGE,"E120"),sQuery(id+"F27.wireOp",EDGE,"E123")])]});
            extrude(context, id + "F32", {"entities" : qUnion([Q0, Q1, Q2, Q3]), "operationType" : NewBodyOperationType.ADD, "endBound" : BoundingType.UP_TO_SURFACE, "oppositeDirection" : true, "depth" : 25.4 * mm, "endBoundEntityFace" : qUnion([Q4]), "offsetDistance" : 25.4 * mm});
        }
        {
            var Q0;
            Q0=makeQuery(id+"F31.imprint","IMPRINT",FACE,{"disambiguationData":[TD([[makeQuery(id+"F31.imprint","IMPRINT",EDGE,{"derivedFrom":sQuery(id+"F31.wireOp",EDGE,"E133.0")}),1.0]])]});
            var Q1;
            Q1=makeQuery(id+"F31.imprint","IMPRINT",FACE,{"disambiguationData":[TD([[makeQuery(id+"F31.imprint","IMPRINT",EDGE,{"derivedFrom":sQuery(id+"F31.wireOp",EDGE,"E133.0")}),-1.0]])]});
            var Q2;
            Q2=makeQuery(id+"F31.imprint","IMPRINT",FACE,{"disambiguationData":[TD([[makeQuery(id+"F31.imprint","IMPRINT",EDGE,{"derivedFrom":sQuery(id+"F31.wireOp",EDGE,"E135.0")}),-1.0]])]});
            var Q3;
            {var subQ0=sQuery(id+"F31.wireOp",EDGE,"E149.0.3");Q3=makeQuery(id+"F31.imprint","IMPRINT",FACE,{"disambiguationData":[TD([[makeQuery(id+"F31.imprint","IMPRINT",EDGE,{"derivedFrom":subQ0}),1.0]])]});}
            var Q4;
            {var subQ5=sQuery(id+"F31.wireOp",EDGE,"E142.2");var subQ7=makeQuery(id+"F31.imprint","INTERSECT",VERTEX,{"derivedFrom":[subQ5,sQuery(id+"F31.wireOp",EDGE,"E144")]});Q4=makeQuery(id+"F31.imprint","IMPRINT",FACE,{"disambiguationData":[TD([[makeQuery(id+"F31.imprint","IMPRINT",EDGE,{"disambiguationData":[TD([[subQ7,1.0]])],"derivedFrom":subQ5}),1.0]])]});}
            var Q5;
            Q5=makeQuery(id+"F31.imprint","IMPRINT",FACE,{"disambiguationData":[TD([[makeQuery(id+"F31.imprint","IMPRINT",EDGE,{"derivedFrom":sQuery(id+"F31.wireOp",EDGE,"E134.0")}),1.0]])]});
            var Q6;
            {var subQ0=sQuery(id+"F31.wireOp",EDGE,"E149.0.2");var subQ1=sQuery(id+"F31.wireOp",EDGE,"E142.1");var subQ2=makeQuery(id+"F31.imprint","INTERSECT",VERTEX,{"derivedFrom":[subQ1,subQ0]});Q6=makeQuery(id+"F31.imprint","IMPRINT",FACE,{"disambiguationData":[TD([[makeQuery(id+"F31.imprint","IMPRINT",EDGE,{"disambiguationData":[TD([[subQ2,-1.0]])],"derivedFrom":subQ1}),1.0]])]});}
            extrude(context, id + "F33", {"entities" : qUnion([Q0, Q1, Q2, Q3, Q4, Q5, Q6]), "operationType" : NewBodyOperationType.ADD, "endBound" : BoundingType.UP_TO_NEXT, "oppositeDirection" : true, "depth" : 25.4 * mm, "offsetDistance" : 25.4 * mm});
        }
        {
            var Q0;
            Q0=makeQuery(id+"F32.opExtrude","CAP_FACE",FACE,{"disambiguationData":[OSD([sQuery(id+"F31.wireOp",EDGE,"E148.0.0"),sQuery(id+"F31.wireOp",EDGE,"E148.0.1"),sQuery(id+"F31.wireOp",EDGE,"E148.0.2"),sQuery(id+"F31.wireOp",EDGE,"E148.0.3")])],"isStart":true});
            cPlane(context, id + "F34", {"entities" : qUnion([Q0]), "cplaneType" : CPlaneType.OFFSET, "offset" : 10.16 * mm, "oppositeDirection" : true, "width" : 152.4 * mm, "height" : 152.4 * mm});
        }
        {
            var Q0;
            Q0=qCreatedBy(id+"F34.planeOp",FACE);
            var sketch = newSketch(context, id + "F35", { "sketchPlane" : qUnion([Q0])});
            skPoint(sketch, "E154.0", {"position": v(11.94, -12.7) * mm});
            skLineSegment(sketch, "E155.0.0", {"start": v(17.02, -2.49) * mm, "end": v(12.57, -5.05) * mm});
            skLineSegment(sketch, "E155.0.1", {"start": v(12.57, -5.05) * mm, "end": v(12.57, -10.19) * mm});
            skLineSegment(sketch, "E155.0.2", {"start": v(12.57, -10.19) * mm, "end": v(16.93, -12.7) * mm});
            skFitSpline(sketch, "E155.0.3", {"points": [v(11.94, -12.7) * mm, v(17.44, -12.7) * mm, v(22.95, -12.7) * mm, v(28.46, -12.7) * mm]});
            skLineSegment(sketch, "E155.0.4", {"start": v(17.1, -12.7) * mm, "end": v(21.46, -10.19) * mm});
            skLineSegment(sketch, "E155.0.5", {"start": v(21.46, -10.19) * mm, "end": v(21.46, -5.05) * mm});
            skLineSegment(sketch, "E155.0.6", {"start": v(21.46, -5.05) * mm, "end": v(17.02, -2.49) * mm});
            skFitSpline(sketch, "E156.0.0", {"points": [v(53.21, -6.42) * mm, v(53.21, -7.64) * mm, v(53.21, -8.87) * mm, v(53.21, -10.09) * mm]});
            skLineSegment(sketch, "E156.0.1", {"start": v(53.21, -10.09) * mm, "end": v(53.21, -11.55) * mm});
            skLineSegment(sketch, "E156.0.2", {"start": v(53.21, -11.55) * mm, "end": v(55.2, -12.7) * mm});
            skFitSpline(sketch, "E156.0.3", {"points": [v(51.26, -12.7) * mm, v(54.24, -12.7) * mm, v(57.22, -12.7) * mm, v(60.2, -12.7) * mm]});
            skLineSegment(sketch, "E156.0.4", {"start": v(57.58, -12.7) * mm, "end": v(60.2, -11.19) * mm});
            skFitSpline(sketch, "E156.0.5", {"points": [v(60.2, -12.7) * mm, v(60.2, -8.55) * mm, v(60.2, -4.4) * mm, v(60.2, -0.25) * mm]});
            skLineSegment(sketch, "E156.0.6", {"start": v(60.2, -5.32) * mm, "end": v(56.39, -3.12) * mm});
            skLineSegment(sketch, "E156.0.7", {"start": v(56.39, -3.12) * mm, "end": v(53.21, -4.96) * mm});
            skLineSegment(sketch, "E156.0.8", {"start": v(53.21, -4.96) * mm, "end": v(53.21, -6.42) * mm});
            skLineSegment(sketch, "E157", {"start": v(12.57, -10.19) * mm, "end": v(21.46, -5.05) * mm});
            skCircle(sketch, "E158.cCircle", {"center": v(17.02, -7.62) * mm, "radius": 3.18 * mm, "construction": true});
            skLineSegment(sketch, "E158.0", {"start": v(20.2, -5.79) * mm, "end": v(20.2, -9.45) * mm});
            skLineSegment(sketch, "E158.1", {"start": v(20.2, -9.45) * mm, "end": v(17.02, -11.29) * mm});
            skLineSegment(sketch, "E158.2", {"start": v(17.02, -11.29) * mm, "end": v(13.84, -9.45) * mm});
            skLineSegment(sketch, "E158.3", {"start": v(13.84, -9.45) * mm, "end": v(13.84, -5.79) * mm});
            skLineSegment(sketch, "E158.4", {"start": v(13.84, -5.79) * mm, "end": v(17.02, -3.95) * mm});
            skLineSegment(sketch, "E158.5", {"start": v(17.02, -3.95) * mm, "end": v(20.2, -5.79) * mm});
            skPoint(sketch, "E158.0.midPoint", {"position": v(20.2, -7.62) * mm});
            skCircle(sketch, "E159.cCircle", {"center": v(56.39, -8.26) * mm, "radius": 3.18 * mm, "construction": true});
            skLineSegment(sketch, "E159.0", {"start": v(59.56, -6.42) * mm, "end": v(59.56, -10.09) * mm});
            skLineSegment(sketch, "E159.1", {"start": v(59.56, -10.09) * mm, "end": v(56.39, -11.92) * mm});
            skLineSegment(sketch, "E159.2", {"start": v(56.39, -11.92) * mm, "end": v(53.21, -10.09) * mm});
            skLineSegment(sketch, "E159.3", {"start": v(53.21, -10.09) * mm, "end": v(53.21, -6.42) * mm});
            skLineSegment(sketch, "E159.4", {"start": v(53.21, -6.42) * mm, "end": v(56.39, -4.59) * mm});
            skLineSegment(sketch, "E159.5", {"start": v(56.39, -4.59) * mm, "end": v(59.56, -6.42) * mm});
            skPoint(sketch, "E159.0.midPoint", {"position": v(59.56, -8.26) * mm});
            skSolve(sketch);
        }
        {
            var Q0;
            Q0=makeQuery(id+"F35.imprint","IMPRINT",FACE,{"disambiguationData":[TD([[makeQuery(id+"F35.imprint","IMPRINT",EDGE,{"derivedFrom":sQuery(id+"F35.wireOp",EDGE,"E159.0")}),-1.0]])]});
            var Q1;
            {var subQ2=sQuery(id+"F35.wireOp",EDGE,"E158.3");Q1=makeQuery(id+"F35.imprint","IMPRINT",FACE,{"disambiguationData":[TD([[makeQuery(id+"F35.imprint","IMPRINT",EDGE,{"derivedFrom":subQ2}),-1.0]])]});}
            var Q2;
            {var subQ0=sQuery(id+"F35.wireOp",EDGE,"E158.0");Q2=makeQuery(id+"F35.imprint","IMPRINT",FACE,{"disambiguationData":[TD([[makeQuery(id+"F35.imprint","IMPRINT",EDGE,{"derivedFrom":subQ0}),-1.0]])]});}
            extrude(context, id + "F36", {"entities" : qUnion([Q0, Q1, Q2]), "operationType" : NewBodyOperationType.REMOVE, "depth" : 8.25 * mm, "offsetDistance" : 25.4 * mm});
        }
        {
            var Q0;
            Q0=makeQuery(id+"F31.imprint","IMPRINT",FACE,{"disambiguationData":[TD([[makeQuery(id+"F31.imprint","IMPRINT",EDGE,{"derivedFrom":sQuery(id+"F31.wireOp",EDGE,"E150.0.0")}),1.0]])]});
            extrude(context, id + "F37", {"entities" : qUnion([Q0]), "operationType" : NewBodyOperationType.ADD, "endBound" : BoundingType.UP_TO_NEXT, "oppositeDirection" : true, "depth" : 25.4 * mm, "offsetDistance" : 25.4 * mm});
        }
        {
            var Q0;
            Q0=makeQuery(id+"F31.imprint","IMPRINT",FACE,{"disambiguationData":[TD([[makeQuery(id+"F31.imprint","IMPRINT",EDGE,{"derivedFrom":sQuery(id+"F31.wireOp",EDGE,"E151.0.0")}),1.0]])]});
            var Q1;
            Q1=makeQuery(id+"F29.opLoft","SWEPT_FACE",FACE,{"disambiguationData":[OSD([sQuery(id+"F26.wireOp",EDGE,"E113"),sQuery(id+"F26.wireOp",EDGE,"E117"),sQuery(id+"F26.wireOp",EDGE,"E118"),sQuery(id+"F27.wireOp",EDGE,"E120"),sQuery(id+"F27.wireOp",EDGE,"E121"),sQuery(id+"F27.wireOp",EDGE,"E122")])]});
            extrude(context, id + "F38", {"entities" : qUnion([Q0]), "operationType" : NewBodyOperationType.ADD, "endBound" : BoundingType.UP_TO_SURFACE, "oppositeDirection" : true, "depth" : 25.4 * mm, "endBoundEntityFace" : qUnion([Q1]), "offsetDistance" : 25.4 * mm});
        }
        {
            var Q0;
            Q0=makeQuery(id+"F31.imprint","IMPRINT",FACE,{"disambiguationData":[TD([[makeQuery(id+"F31.imprint","IMPRINT",EDGE,{"derivedFrom":sQuery(id+"F31.wireOp",EDGE,"E152.0.0")}),1.0]])]});
            extrude(context, id + "F39", {"entities" : qUnion([Q0]), "operationType" : NewBodyOperationType.ADD, "endBound" : BoundingType.UP_TO_NEXT, "oppositeDirection" : true, "depth" : 25.4 * mm, "offsetDistance" : 25.4 * mm});
        }
        {
            var Q0;
            Q0=makeQuery(id+"F31.imprint","IMPRINT",FACE,{"disambiguationData":[TD([[makeQuery(id+"F31.imprint","IMPRINT",EDGE,{"derivedFrom":sQuery(id+"F31.wireOp",EDGE,"E153.0.0")}),1.0]])]});
            extrude(context, id + "F40", {"entities" : qUnion([Q0]), "operationType" : NewBodyOperationType.ADD, "endBound" : BoundingType.UP_TO_NEXT, "oppositeDirection" : true, "depth" : 25.4 * mm, "offsetDistance" : 25.4 * mm});
        }
        {
            var Q0;
            Q0=makeQuery(id+"F32.opExtrude","CAP_FACE",FACE,{"disambiguationData":[OSD([sQuery(id+"F31.wireOp",EDGE,"E148.0.0"),sQuery(id+"F31.wireOp",EDGE,"E148.0.1"),sQuery(id+"F31.wireOp",EDGE,"E148.0.2"),sQuery(id+"F31.wireOp",EDGE,"E148.0.3")])],"isStart":true});
            var sketch = newSketch(context, id + "F41", { "sketchPlane" : qUnion([Q0])});
            skLineSegment(sketch, "E160.0.0", {"start": v(17.02, -3.95) * mm, "end": v(20.2, -5.79) * mm});
            skLineSegment(sketch, "E160.0.1", {"start": v(20.2, -5.79) * mm, "end": v(20.2, -9.45) * mm});
            skLineSegment(sketch, "E160.0.2", {"start": v(20.2, -9.45) * mm, "end": v(17.02, -11.29) * mm});
            skLineSegment(sketch, "E160.0.3", {"start": v(17.02, -11.29) * mm, "end": v(13.84, -9.45) * mm});
            skLineSegment(sketch, "E160.0.4", {"start": v(13.84, -9.45) * mm, "end": v(13.84, -5.79) * mm});
            skLineSegment(sketch, "E160.0.5", {"start": v(13.84, -5.79) * mm, "end": v(17.02, -3.95) * mm});
            skLineSegment(sketch, "E161.0.0", {"start": v(53.21, -6.42) * mm, "end": v(56.39, -4.59) * mm});
            skLineSegment(sketch, "E161.0.1", {"start": v(56.39, -4.59) * mm, "end": v(59.56, -6.42) * mm});
            skLineSegment(sketch, "E161.0.2", {"start": v(59.56, -6.42) * mm, "end": v(59.56, -10.09) * mm});
            skLineSegment(sketch, "E161.0.3", {"start": v(59.56, -10.09) * mm, "end": v(56.39, -11.92) * mm});
            skLineSegment(sketch, "E161.0.4", {"start": v(56.39, -11.92) * mm, "end": v(53.21, -10.09) * mm});
            skLineSegment(sketch, "E161.0.5", {"start": v(53.21, -10.09) * mm, "end": v(53.21, -6.42) * mm});
            skLineSegment(sketch, "E162", {"start": v(13.84, -5.79) * mm, "end": v(20.2, -9.45) * mm});
            skLineSegment(sketch, "E163", {"start": v(53.21, -6.42) * mm, "end": v(59.56, -10.09) * mm});
            skCircle(sketch, "E164", {"center": v(17.02, -7.62) * mm, "radius": 1.75 * mm});
            skCircle(sketch, "E165", {"center": v(56.39, -8.26) * mm, "radius": 1.75 * mm});
            skSolve(sketch);
        }
        {
            var Q0;
            {var subQ0=sQuery(id+"F41.wireOp",EDGE,"E164");var subQ1=sQuery(id+"F41.wireOp",EDGE,"E162");var subQ2=makeQuery(id+"F41.imprint","INTERSECT",VERTEX,{"disambiguationData":[OD(0.0)],"derivedFrom":[subQ1,subQ0]});Q0=makeQuery(id+"F41.imprint","IMPRINT",FACE,{"disambiguationData":[TD([[makeQuery(id+"F41.imprint","IMPRINT",EDGE,{"disambiguationData":[TD([[subQ2,-1.0]])],"derivedFrom":subQ1}),-1.0]])]});}
            var Q1;
            {var subQ0=sQuery(id+"F41.wireOp",EDGE,"E164");var subQ1=sQuery(id+"F41.wireOp",EDGE,"E162");var subQ2=makeQuery(id+"F41.imprint","INTERSECT",VERTEX,{"disambiguationData":[OD(0.0)],"derivedFrom":[subQ1,subQ0]});Q1=makeQuery(id+"F41.imprint","IMPRINT",FACE,{"disambiguationData":[TD([[makeQuery(id+"F41.imprint","IMPRINT",EDGE,{"disambiguationData":[TD([[subQ2,-1.0]])],"derivedFrom":subQ1}),1.0]])]});}
            var Q2;
            {var subQ0=sQuery(id+"F41.wireOp",EDGE,"E165");var subQ1=sQuery(id+"F41.wireOp",EDGE,"E163");var subQ2=makeQuery(id+"F41.imprint","INTERSECT",VERTEX,{"disambiguationData":[OD(0.0)],"derivedFrom":[subQ1,subQ0]});Q2=makeQuery(id+"F41.imprint","IMPRINT",FACE,{"disambiguationData":[TD([[makeQuery(id+"F41.imprint","IMPRINT",EDGE,{"disambiguationData":[TD([[subQ2,-1.0]])],"derivedFrom":subQ1}),-1.0]])]});}
            var Q3;
            {var subQ0=sQuery(id+"F41.wireOp",EDGE,"E165");var subQ1=sQuery(id+"F41.wireOp",EDGE,"E163");var subQ2=makeQuery(id+"F41.imprint","INTERSECT",VERTEX,{"disambiguationData":[OD(0.0)],"derivedFrom":[subQ1,subQ0]});Q3=makeQuery(id+"F41.imprint","IMPRINT",FACE,{"disambiguationData":[TD([[makeQuery(id+"F41.imprint","IMPRINT",EDGE,{"disambiguationData":[TD([[subQ2,-1.0]])],"derivedFrom":subQ1}),1.0]])]});}
            extrude(context, id + "F42", {"entities" : qUnion([Q0, Q1, Q2, Q3]), "operationType" : NewBodyOperationType.REMOVE, "endBound" : BoundingType.THROUGH_ALL, "oppositeDirection" : true, "depth" : 25.4 * mm, "offsetDistance" : 25.4 * mm});
        }
    });
